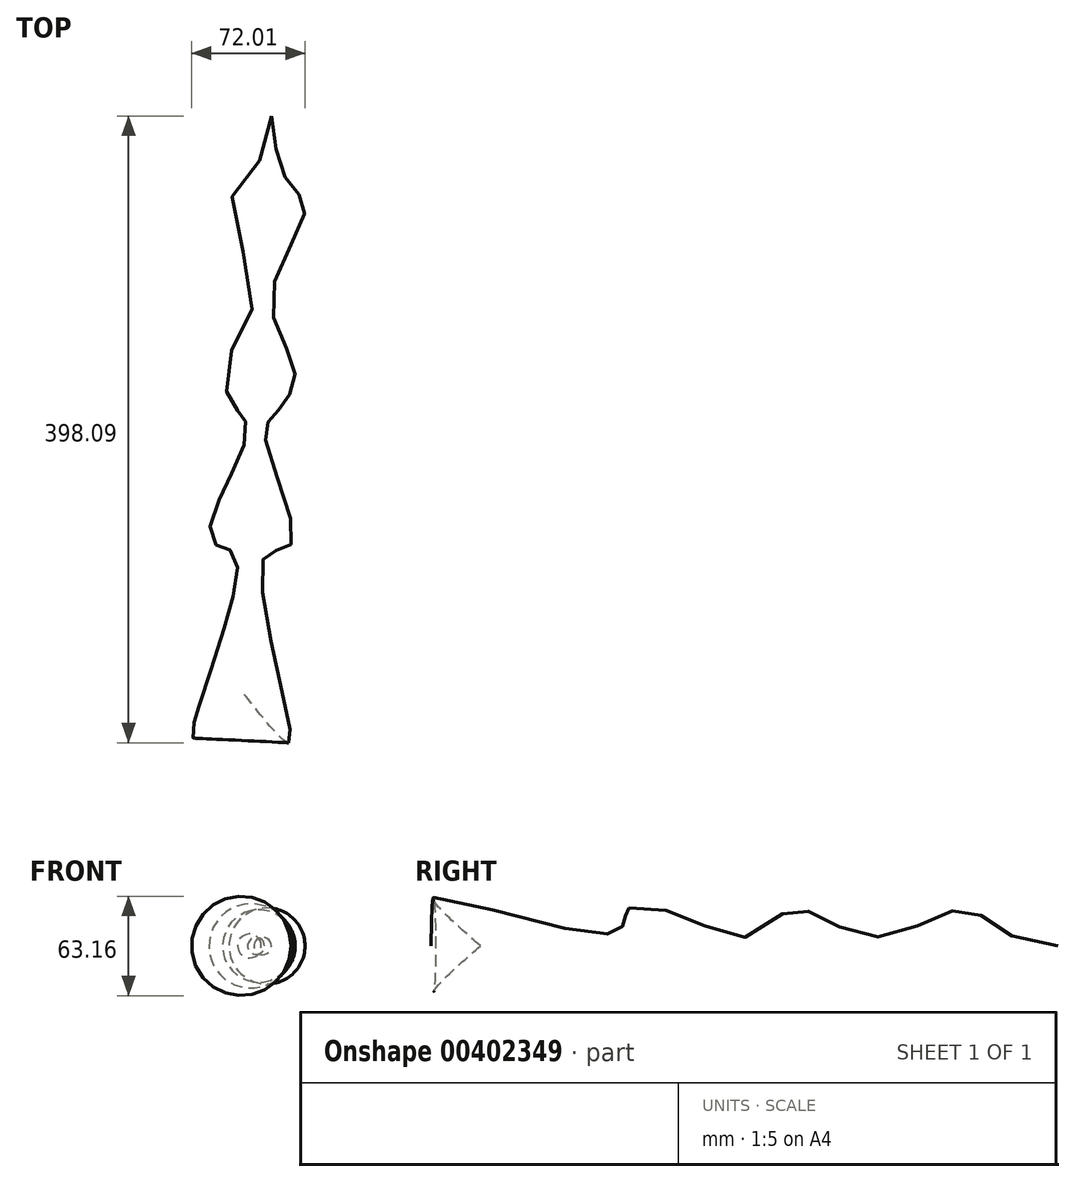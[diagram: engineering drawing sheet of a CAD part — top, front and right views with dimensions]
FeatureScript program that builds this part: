
annotation { "Feature Type Name" : "Feature", "Feature Type Description" : "" }
export const myFeature = defineFeature(function(context is Context, id is Id, definition is map)
    precondition{}
    {
        {
            var Q0;
            Q0=qCreatedBy(makeId("Top.planeOp"),FACE);
            var sketch = newSketch(context, id + "F0", { "sketchPlane" : qUnion([Q0])});
            skLineSegment(sketch, "E0", {"start": v(-21.33, 366.62) * mm, "end": v(-39.14, 0) * mm});
            skFitSpline(sketch, "E1", {"points": [v(-21.33, 366.62) * mm, v(-10.77, 324.38) * mm, v(0, 307.77) * mm, v(-21.33, 250.62) * mm, v(-6.54, 205.06) * mm, v(-12.52, 185.75) * mm, v(-21.33, 174.66) * mm, v(-25.57, 163.42) * mm, v(-7.56, 98.24) * mm, v(-16.84, 90.9) * mm, v(-26.64, 84.93) * mm, v(-12.34, -8.79) * mm, v(-10.4, -31.47) * mm, v(-39.14, 0) * mm], "startDerivative": vector(67.7, -548.74) * mm, "endDerivative": vector(-419.3, 534.14) * mm});
            skSolve(sketch);
        }
        {
            var Q0;
            Q0=makeQuery(id+"F0.imprint","IMPRINT",FACE,{"disambiguationData":[TD([[makeQuery(id+"F0.imprint","IMPRINT",EDGE,{"derivedFrom":sQuery(id+"F0.wireOp",EDGE,"E0")}),1.0]])]});
            var Q1;
            Q1=sQuery(id+"F0.wireOp",EDGE,"E0");
            revolve(context, id + "F1", {"entities" : qUnion([Q0]), "axis" : qUnion([Q1]), "revolveType" : RevolveType.FULL});
        }
    });
